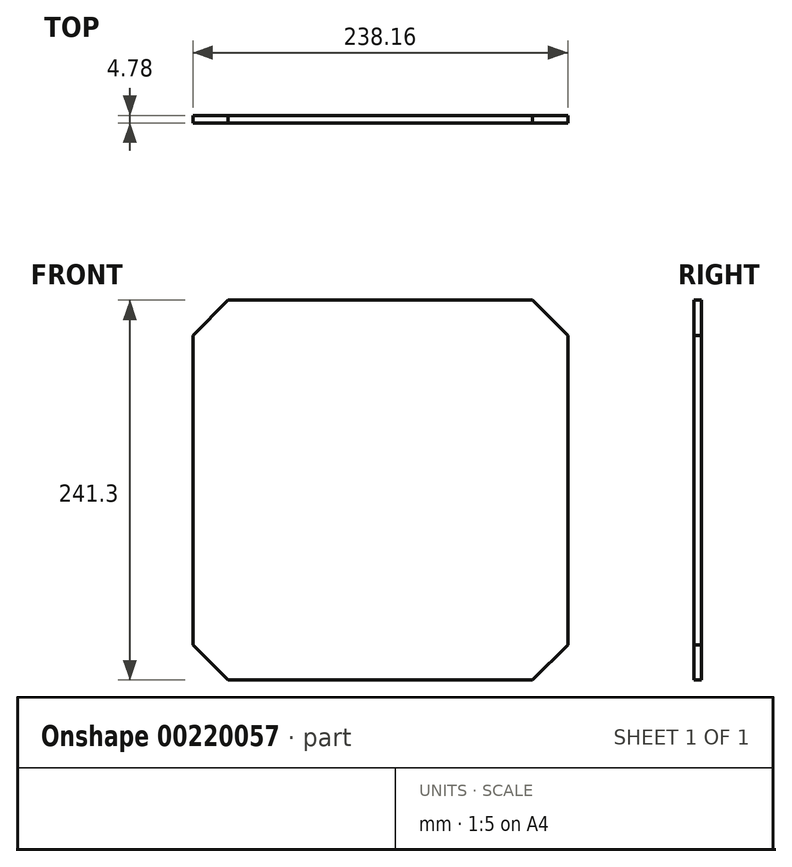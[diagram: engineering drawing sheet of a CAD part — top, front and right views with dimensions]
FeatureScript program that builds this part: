
annotation { "Feature Type Name" : "Feature", "Feature Type Description" : "" }
export const myFeature = defineFeature(function(context is Context, id is Id, definition is map)
    precondition{}
    {
        {
            var Q0;
            Q0=qCreatedBy(makeId("Front.planeOp"),FACE);
            var sketch = newSketch(context, id + "F0", { "sketchPlane" : qUnion([Q0])});
            skLineSegment(sketch, "E0.bottom", {"start": v(119.08, 120.65) * mm, "end": v(-119.08, 120.65) * mm});
            skLineSegment(sketch, "E0.top", {"start": v(119.08, -120.65) * mm, "end": v(-119.08, -120.65) * mm});
            skLineSegment(sketch, "E0.left", {"start": v(119.08, 120.65) * mm, "end": v(119.08, -120.65) * mm});
            skLineSegment(sketch, "E0.right", {"start": v(-119.08, 120.65) * mm, "end": v(-119.08, -120.65) * mm});
            skPoint(sketch, "E0.middle", {"position": v(0, 0) * mm});
            skSolve(sketch);
        }
        {
            var Q0;
            Q0 = qSketchRegion(id + "F0", true);
            extrude(context, id + "F1", {"entities" : qUnion([Q0]), "depth" : 4.78 * mm});
        }
        {
            var Q0;
            Q0=makeQuery(id+"F1.opExtrude","SWEPT_EDGE",EDGE,{"disambiguationData":[OSD([sQuery(id+"F0.wireOp",EDGE,"E0.bottom"),sQuery(id+"F0.wireOp",EDGE,"E0.right")])]});
            var Q1;
            Q1=makeQuery(id+"F1.opExtrude","SWEPT_EDGE",EDGE,{"disambiguationData":[OSD([sQuery(id+"F0.wireOp",EDGE,"E0.bottom"),sQuery(id+"F0.wireOp",EDGE,"E0.left")])]});
            var Q2;
            Q2=makeQuery(id+"F1.opExtrude","SWEPT_EDGE",EDGE,{"disambiguationData":[OSD([sQuery(id+"F0.wireOp",EDGE,"E0.top"),sQuery(id+"F0.wireOp",EDGE,"E0.left")])]});
            var Q3;
            Q3=makeQuery(id+"F1.opExtrude","SWEPT_EDGE",EDGE,{"disambiguationData":[OSD([sQuery(id+"F0.wireOp",EDGE,"E0.top"),sQuery(id+"F0.wireOp",EDGE,"E0.right")])]});
            chamfer(context, id + "F2", {"entities" : qUnion([Q0, Q1, Q2, Q3]), "width" : 22.35 * mm, "tangentPropagation" : true});
        }
    });
